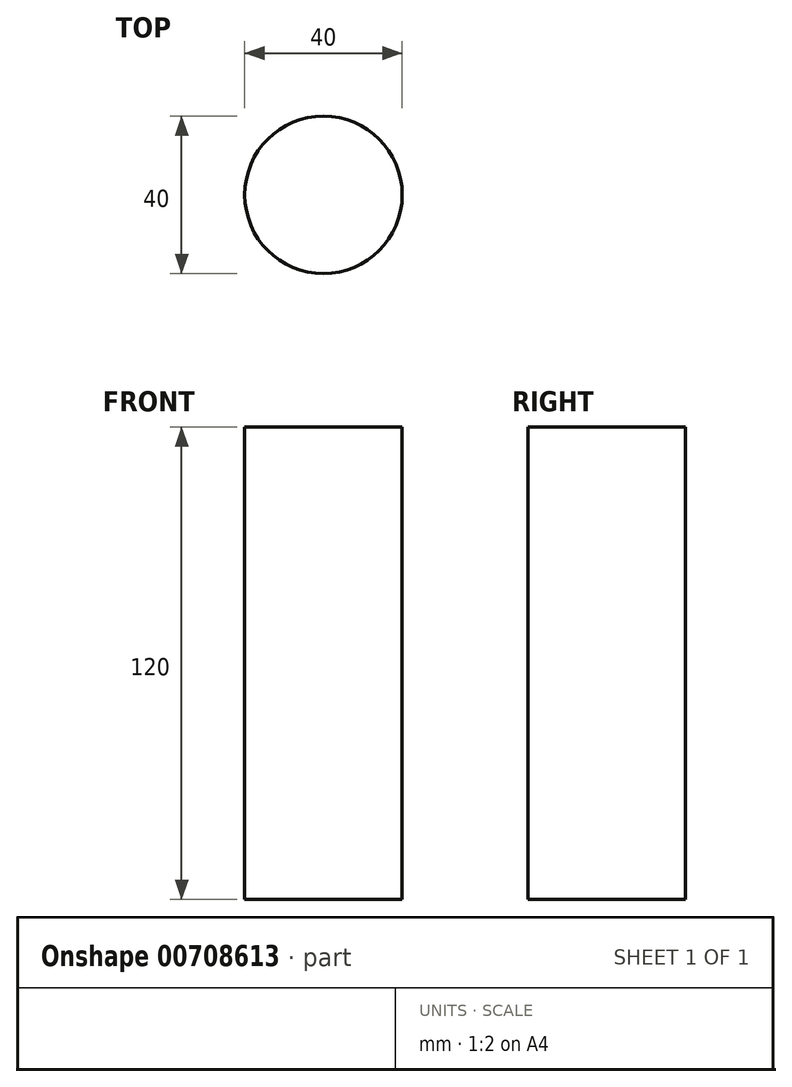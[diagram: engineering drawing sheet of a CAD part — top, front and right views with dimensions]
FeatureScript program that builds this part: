
annotation { "Feature Type Name" : "Feature", "Feature Type Description" : "" }
export const myFeature = defineFeature(function(context is Context, id is Id, definition is map)
    precondition{}
    {
        {
            var Q0;
            Q0=qCreatedBy(makeId("Top.planeOp"),FACE);
            var sketch = newSketch(context, id + "F0", { "sketchPlane" : qUnion([Q0])});
            skCircle(sketch, "E0", {"center": v(0, 0) * mm, "radius": 20 * mm});
            skSolve(sketch);
        }
        {
            var Q0;
            Q0=makeQuery(id+"F0.imprint","IMPRINT",FACE,{"disambiguationData":[TD([[makeQuery(id+"F0.imprint","IMPRINT",EDGE,{"derivedFrom":sQuery(id+"F0.wireOp",EDGE,"E0")}),1.0]])]});
            extrude(context, id + "F1", {"entities" : qUnion([Q0]), "depth" : 120 * mm, "offsetDistance" : 25 * mm});
        }
    });
